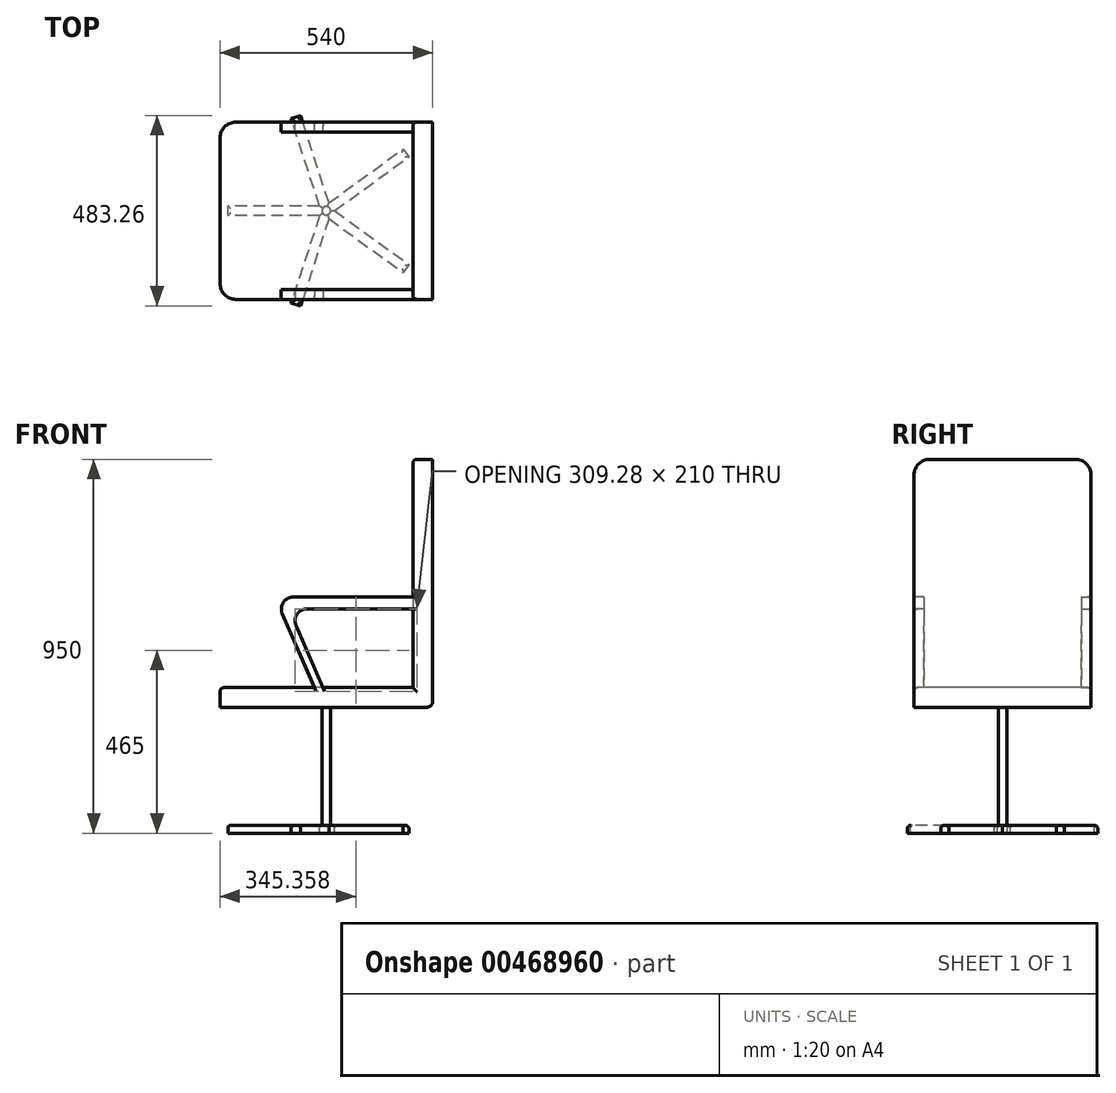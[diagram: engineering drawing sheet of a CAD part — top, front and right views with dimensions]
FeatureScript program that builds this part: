
annotation { "Feature Type Name" : "Feature", "Feature Type Description" : "" }
export const myFeature = defineFeature(function(context is Context, id is Id, definition is map)
    precondition{}
    {
        {
            var Q0;
            Q0=qCreatedBy(makeId("Front.planeOp"),FACE);
            var sketch = newSketch(context, id + "F0", { "sketchPlane" : qUnion([Q0])});
            skLineSegment(sketch, "E0", {"start": v(0, 0) * mm, "end": v(-250, 0) * mm});
            skLineSegment(sketch, "E1", {"start": v(-250, 0) * mm, "end": v(-250, 20) * mm});
            skLineSegment(sketch, "E2", {"start": v(0, 0) * mm, "end": v(0, 20) * mm});
            skLineSegment(sketch, "E3", {"start": v(0, 20) * mm, "end": v(-250, 20) * mm});
            skSolve(sketch);
        }
        {
            var Q0;
            Q0 = qSketchRegion(id + "F0", true);
            extrude(context, id + "F1", {"entities" : qUnion([Q0]), "endBound" : BoundingType.SYMMETRIC, "depth" : 25 * mm});
        }
        {
            var Q0;
            Q0=makeQuery(id+"F1.opExtrude","CAP_EDGE",EDGE,{"disambiguationData":[OSD([sQuery(id+"F0.wireOp",EDGE,"E3")])],"isStart":false});
            var Q1;
            Q1=makeQuery(id+"F1.opExtrude","SWEPT_EDGE",EDGE,{"disambiguationData":[OSD([sQuery(id+"F0.wireOp",EDGE,"E1"),sQuery(id+"F0.wireOp",EDGE,"E3")])]});
            var Q2;
            Q2=makeQuery(id+"F1.opExtrude","CAP_EDGE",EDGE,{"disambiguationData":[OSD([sQuery(id+"F0.wireOp",EDGE,"E3")])],"isStart":true});
            fillet(context, id + "F2", {"entities" : qUnion([Q0, Q1, Q2]), "radius" : 7 * mm, "tangentPropagation" : true, "allowEdgeOverflow" : false});
        }
        {
            var Q0;
            Q0=qCreatedBy(makeId("Front.planeOp"),FACE);
            var sketch = newSketch(context, id + "F3", { "sketchPlane" : qUnion([Q0])});
            skLineSegment(sketch, "E4", {"start": v(0, 0) * mm, "end": v(0, 122.93) * mm, "construction": true});
            skSolve(sketch);
        }
        {
            var Q0;
            Q0=makeQuery(id+"F1.opExtrude","SWEPT_BODY",BODY,{"disambiguationData":[OSD([sQuery(id+"F0.wireOp",EDGE,"E0"),sQuery(id+"F0.wireOp",EDGE,"E1"),sQuery(id+"F0.wireOp",EDGE,"E2"),sQuery(id+"F0.wireOp",EDGE,"E3")])]});
            var Q1;
            Q1=sQuery(id+"F3.wireOp",EDGE,"E4");
            var Q2;
            Q2=makeQuery(id+"F1.opExtrude","SWEPT_BODY",BODY,{"disambiguationData":[OSD([sQuery(id+"F0.wireOp",EDGE,"E0"),sQuery(id+"F0.wireOp",EDGE,"E1"),sQuery(id+"F0.wireOp",EDGE,"E2"),sQuery(id+"F0.wireOp",EDGE,"E3")])]});
            circularPattern(context, id + "F4", {"operationType" : NewBodyOperationType.ADD, "entities" : qUnion([Q0]), "axis" : qUnion([Q1]), "angle" : 360 * degree, "instanceCount" : 5, "equalSpace" : true});
        }
        {
            var Q0;
            Q0=makeQuery(id+"F1.opExtrude","SWEPT_FACE",FACE,{"disambiguationData":[OSD([sQuery(id+"F0.wireOp",EDGE,"E3")])]});
            var sketch = newSketch(context, id + "F5", { "sketchPlane" : qUnion([Q0])});
            skCircle(sketch, "E5", {"center": v(0, 0) * mm, "radius": 11 * mm});
            skSolve(sketch);
        }
        {
            var Q0;
            Q0 = qSketchRegion(id + "F5", true);
            extrude(context, id + "F6", {"entities" : qUnion([Q0]), "operationType" : NewBodyOperationType.ADD, "depth" : 300 * mm});
        }
        {
            var Q0;
            Q0=makeQuery(id+"F6.opExtrude","CAP_FACE",FACE,{"disambiguationData":[OSD([sQuery(id+"F5.wireOp",EDGE,"E5")])],"isStart":false});
            var sketch = newSketch(context, id + "F7", { "sketchPlane" : qUnion([Q0])});
            skLineSegment(sketch, "E6.bottom", {"start": v(270, 225) * mm, "end": v(-230, 225) * mm});
            skLineSegment(sketch, "E6.top", {"start": v(270, -225) * mm, "end": v(-230, -225) * mm});
            skLineSegment(sketch, "E6.left", {"start": v(270, 225) * mm, "end": v(270, -225) * mm});
            skLineSegment(sketch, "E6.right", {"start": v(-270, 185) * mm, "end": v(-270, -185) * mm});
            skPoint(sketch, "E6.middle", {"position": v(0, 0) * mm});
            skPoint(sketch, "E7.visualSharp", {"position": v(-270, 225) * mm});
            skArc(sketch, "E7.filletArc", {"start": v(-230, 225) * mm, "mid": v(-258.28, 213.28) * mm, "end": v(-270, 185) * mm});
            skPoint(sketch, "E8.visualSharp", {"position": v(-270, -225) * mm});
            skArc(sketch, "E8.filletArc", {"start": v(-270, -185) * mm, "mid": v(-258.28, -213.28) * mm, "end": v(-230, -225) * mm});
            skSolve(sketch);
        }
        {
            var Q0;
            Q0=makeQuery(id+"F7.imprint","IMPRINT",FACE,{"disambiguationData":[TD([[makeQuery(id+"F7.imprint","IMPRINT",EDGE,{"derivedFrom":sQuery(id+"F7.wireOp",EDGE,"E6.bottom")}),1.0]])]});
            var Q1;
            Q1=makeQuery(id+"F7.imprint","IMPRINT",FACE,{"disambiguationData":[TD([[makeQuery(id+"F7.imprint","IMPRINT",EDGE,{"derivedFrom":makeQuery(id+"F6.opExtrude","CAP_EDGE",EDGE,{"disambiguationData":[OSD([sQuery(id+"F5.wireOp",EDGE,"E5")])],"isStart":false})}),1.0]])]});
            extrude(context, id + "F8", {"entities" : qUnion([Q0, Q1]), "operationType" : NewBodyOperationType.ADD, "depth" : 50 * mm});
        }
        {
            var Q0;
            Q0=makeQuery(id+"F8.opExtrude","CAP_FACE",FACE,{"disambiguationData":[OSD([sQuery(id+"F7.wireOp",EDGE,"E6.bottom"),sQuery(id+"F7.wireOp",EDGE,"E6.top"),sQuery(id+"F7.wireOp",EDGE,"E6.left"),sQuery(id+"F7.wireOp",EDGE,"E6.right"),sQuery(id+"F7.wireOp",EDGE,"E7.filletArc"),sQuery(id+"F7.wireOp",EDGE,"E8.filletArc")])],"isStart":false});
            var sketch = newSketch(context, id + "F9", { "sketchPlane" : qUnion([Q0])});
            skLineSegment(sketch, "E9.bottom", {"start": v(270, 225) * mm, "end": v(220, 225) * mm});
            skLineSegment(sketch, "E9.top", {"start": v(270, -225) * mm, "end": v(220, -225) * mm});
            skLineSegment(sketch, "E9.left", {"start": v(270, 225) * mm, "end": v(270, -225) * mm});
            skLineSegment(sketch, "E9.right", {"start": v(220, 225) * mm, "end": v(220, -225) * mm});
            skSolve(sketch);
        }
        {
            var Q0;
            Q0=makeQuery(id+"F9.imprint","IMPRINT",FACE,{"disambiguationData":[TD([[makeQuery(id+"F9.imprint","IMPRINT",EDGE,{"derivedFrom":sQuery(id+"F9.wireOp",EDGE,"E9.bottom")}),1.0]])]});
            extrude(context, id + "F10", {"entities" : qUnion([Q0]), "operationType" : NewBodyOperationType.ADD, "depth" : 580 * mm});
        }
        {
            var Q0;
            Q0=makeQuery(id+"F10.boolean.opBoolean","MERGE",FACE,{"derivedFrom":[makeQuery(id+"F8.opExtrude","SWEPT_FACE",FACE,{"disambiguationData":[OSD([sQuery(id+"F7.wireOp",EDGE,"E6.top")])]}),makeQuery(id+"F10.opExtrude","SWEPT_FACE",FACE,{"disambiguationData":[OSD([sQuery(id+"F9.wireOp",EDGE,"E9.top")])]})]});
            var sketch = newSketch(context, id + "F11", { "sketchPlane" : qUnion([Q0])});
            skLineSegment(sketch, "E10", {"start": v(220, 600) * mm, "end": v(-84.24, 600) * mm});
            skLineSegment(sketch, "E11", {"start": v(-111.76, 558.04) * mm, "end": v(-30, 370) * mm});
            skLineSegment(sketch, "E12", {"start": v(-30, 370) * mm, "end": v(-8.2, 370) * mm});
            skLineSegment(sketch, "E13", {"start": v(-8.2, 370) * mm, "end": v(-76.9, 528.04) * mm});
            skLineSegment(sketch, "E14", {"start": v(-49.4, 570) * mm, "end": v(220, 570) * mm});
            skLineSegment(sketch, "E15", {"start": v(220, 570) * mm, "end": v(220, 600) * mm});
            skPoint(sketch, "E16.visualSharp", {"position": v(-95.15, 570) * mm});
            skArc(sketch, "E16.filletArc", {"start": v(-49.4, 570) * mm, "mid": v(-74.48, 556.45) * mm, "end": v(-76.9, 528.04) * mm});
            skPoint(sketch, "E17.visualSharp", {"position": v(-130, 600) * mm});
            skArc(sketch, "E17.filletArc", {"start": v(-84.24, 600) * mm, "mid": v(-109.33, 586.45) * mm, "end": v(-111.76, 558.04) * mm});
            skSolve(sketch);
        }
        {
            var Q0;
            Q0=makeQuery(id+"F11.imprint","IMPRINT",FACE,{"disambiguationData":[TD([[makeQuery(id+"F11.imprint","IMPRINT",EDGE,{"derivedFrom":sQuery(id+"F11.wireOp",EDGE,"E10")}),1.0]])]});
            extrude(context, id + "F12", {"entities" : qUnion([Q0]), "oppositeDirection" : true, "depth" : 25 * mm});
        }
        {
            var Q0;
            Q0=makeQuery(id+"F12.opExtrude","SWEPT_BODY",BODY,{"disambiguationData":[OSD([sQuery(id+"F11.wireOp",EDGE,"E10"),sQuery(id+"F11.wireOp",EDGE,"E11"),sQuery(id+"F11.wireOp",EDGE,"E12"),sQuery(id+"F11.wireOp",EDGE,"E13"),sQuery(id+"F11.wireOp",EDGE,"E14"),sQuery(id+"F11.wireOp",EDGE,"E15"),sQuery(id+"F11.wireOp",EDGE,"E16.filletArc"),sQuery(id+"F11.wireOp",EDGE,"E17.filletArc")])]});
            var Q1;
            Q1=qCreatedBy(makeId("Front.planeOp"),FACE);
            mirror(context, id + "F13", {"operationType" : NewBodyOperationType.ADD, "entities" : qUnion([Q0]), "mirrorPlane" : qUnion([Q1])});
        }
        {
            var Q0;
            Q0=makeQuery(id+"F10.opExtrude","CAP_EDGE",EDGE,{"disambiguationData":[OSD([sQuery(id+"F9.wireOp",EDGE,"E9.top")])],"isStart":false});
            var Q1;
            Q1=makeQuery(id+"F10.opExtrude","CAP_EDGE",EDGE,{"disambiguationData":[OSD([sQuery(id+"F9.wireOp",EDGE,"E9.bottom")])],"isStart":false});
            fillet(context, id + "F14", {"entities" : qUnion([Q0, Q1]), "radius" : 40 * mm, "tangentPropagation" : true, "allowEdgeOverflow" : false});
        }
        {
            var Q0;
            Q0=makeQuery(id+"F10.opExtrude","CAP_EDGE",EDGE,{"disambiguationData":[OSD([sQuery(id+"F9.wireOp",EDGE,"E9.right")])],"isStart":false});
            var Q1;
            Q1=makeQuery(id+"F14.opFillet","BLEND_EDGE",EDGE,{"blendedFrom":[makeQuery(id+"F10.opExtrude","CAP_EDGE",EDGE,{"disambiguationData":[OSD([sQuery(id+"F9.wireOp",EDGE,"E9.top")])],"isStart":false}),makeQuery(id+"F10.opExtrude","SWEPT_FACE",FACE,{"disambiguationData":[OSD([sQuery(id+"F9.wireOp",EDGE,"E9.right")])]})],"blendedInto":[makeQuery(id+"F10.opExtrude","SWEPT_FACE",FACE,{"disambiguationData":[OSD([sQuery(id+"F9.wireOp",EDGE,"E9.right")])]})]});
            var Q2;
            {var subQ0=sQuery(id+"F9.wireOp",EDGE,"E9.right");var subQ1=sQuery(id+"F11.wireOp",EDGE,"E10");var subQ2=sQuery(id+"F9.wireOp",EDGE,"E9.top");var subQ3=sQuery(id+"F7.wireOp",EDGE,"E6.top");Q2=makeQuery(id+"F13.boolean.opBoolean","SPLIT",EDGE,{"disambiguationData":[TD([makeQuery(id+"F12.opExtrude","SWEPT_FACE",FACE,{"disambiguationData":[OSD([subQ1])]})])],"derivedFrom":makeQuery(id+"F10.opExtrude","SWEPT_EDGE",EDGE,{"disambiguationData":[OSD([subQ3,subQ2,subQ0])]})});}
            var Q3;
            {var subQ0=sQuery(id+"F9.wireOp",EDGE,"E9.right");var subQ1=sQuery(id+"F9.wireOp",EDGE,"E9.bottom");var subQ2=sQuery(id+"F7.wireOp",EDGE,"E6.bottom");var subQ3=sQuery(id+"F11.wireOp",EDGE,"E10");Q3=makeQuery(id+"F13.boolean.opBoolean","SPLIT",EDGE,{"disambiguationData":[TD([makeQuery(id+"F13.opPattern","COPY",FACE,{"derivedFrom":makeQuery(id+"F12.opExtrude","SWEPT_FACE",FACE,{"disambiguationData":[OSD([subQ3])]}),"instanceName":"1"})])],"derivedFrom":makeQuery(id+"F10.opExtrude","SWEPT_EDGE",EDGE,{"disambiguationData":[OSD([subQ2,subQ1,subQ0])]})});}
            var Q4;
            Q4=makeQuery(id+"F14.opFillet","BLEND_EDGE",EDGE,{"blendedFrom":[makeQuery(id+"F10.opExtrude","CAP_EDGE",EDGE,{"disambiguationData":[OSD([sQuery(id+"F9.wireOp",EDGE,"E9.bottom")])],"isStart":false}),makeQuery(id+"F10.opExtrude","SWEPT_FACE",FACE,{"disambiguationData":[OSD([sQuery(id+"F9.wireOp",EDGE,"E9.right")])]})],"blendedInto":[makeQuery(id+"F10.opExtrude","SWEPT_FACE",FACE,{"disambiguationData":[OSD([sQuery(id+"F9.wireOp",EDGE,"E9.right")])]})]});
            var Q5;
            {var subQ0=sQuery(id+"F9.wireOp",EDGE,"E9.right");var subQ1=sQuery(id+"F9.wireOp",EDGE,"E9.bottom");var subQ2=sQuery(id+"F7.wireOp",EDGE,"E6.bottom");var subQ3=sQuery(id+"F11.wireOp",EDGE,"E14");Q5=makeQuery(id+"F13.boolean.opBoolean","SPLIT",EDGE,{"disambiguationData":[TD([makeQuery(id+"F13.opPattern","COPY",FACE,{"derivedFrom":makeQuery(id+"F12.opExtrude","SWEPT_FACE",FACE,{"disambiguationData":[OSD([subQ3])]}),"instanceName":"1"})])],"derivedFrom":makeQuery(id+"F10.opExtrude","SWEPT_EDGE",EDGE,{"disambiguationData":[OSD([subQ2,subQ1,subQ0])]})});}
            var Q6;
            {var subQ0=sQuery(id+"F9.wireOp",EDGE,"E9.right");var subQ1=sQuery(id+"F7.wireOp",EDGE,"E6.top");var subQ2=sQuery(id+"F9.wireOp",EDGE,"E9.top");var subQ3=sQuery(id+"F11.wireOp",EDGE,"E14");Q6=makeQuery(id+"F13.boolean.opBoolean","SPLIT",EDGE,{"disambiguationData":[TD([makeQuery(id+"F12.opExtrude","SWEPT_FACE",FACE,{"disambiguationData":[OSD([subQ3])]})])],"derivedFrom":makeQuery(id+"F10.opExtrude","SWEPT_EDGE",EDGE,{"disambiguationData":[OSD([subQ1,subQ2,subQ0])]})});}
            var Q7;
            {var subQ0=sQuery(id+"F7.wireOp",EDGE,"E6.top");Q7=makeQuery(id+"F13.boolean.opBoolean","SPLIT",EDGE,{"disambiguationData":[TD([makeQuery(id+"F10.opExtrude","SWEPT_FACE",FACE,{"disambiguationData":[OSD([sQuery(id+"F9.wireOp",EDGE,"E9.right")])]})])],"derivedFrom":makeQuery(id+"F8.opExtrude","CAP_EDGE",EDGE,{"disambiguationData":[OSD([subQ0])],"isStart":false})});}
            var Q8;
            {var subQ0=sQuery(id+"F7.wireOp",EDGE,"E6.top");var subQ1=sQuery(id+"F7.wireOp",EDGE,"E8.filletArc");Q8=makeQuery(id+"F13.boolean.opBoolean","SPLIT",EDGE,{"disambiguationData":[TD([makeQuery(id+"F8.opExtrude","SWEPT_FACE",FACE,{"disambiguationData":[OSD([subQ1])]})])],"derivedFrom":makeQuery(id+"F8.opExtrude","CAP_EDGE",EDGE,{"disambiguationData":[OSD([subQ0])],"isStart":false})});}
            var Q9;
            {var subQ0=sQuery(id+"F7.wireOp",EDGE,"E6.bottom");Q9=makeQuery(id+"F13.boolean.opBoolean","SPLIT",EDGE,{"disambiguationData":[TD([makeQuery(id+"F10.opExtrude","SWEPT_FACE",FACE,{"disambiguationData":[OSD([sQuery(id+"F9.wireOp",EDGE,"E9.right")])]})])],"derivedFrom":makeQuery(id+"F8.opExtrude","CAP_EDGE",EDGE,{"disambiguationData":[OSD([subQ0])],"isStart":false})});}
            fillet(context, id + "F15", {"entities" : qUnion([Q0, Q1, Q2, Q3, Q4, Q5, Q6, Q7, Q8, Q9]), "radius" : 10 * mm, "tangentPropagation" : true, "allowEdgeOverflow" : false});
        }
        {
            var Q0;
            Q0=makeQuery(id+"F8.opExtrude","CAP_EDGE",EDGE,{"disambiguationData":[OSD([sQuery(id+"F7.wireOp",EDGE,"E6.left")])],"isStart":true});
            fillet(context, id + "F16", {"entities" : qUnion([Q0]), "radius" : 15 * mm, "tangentPropagation" : true, "allowEdgeOverflow" : false});
        }
    });
